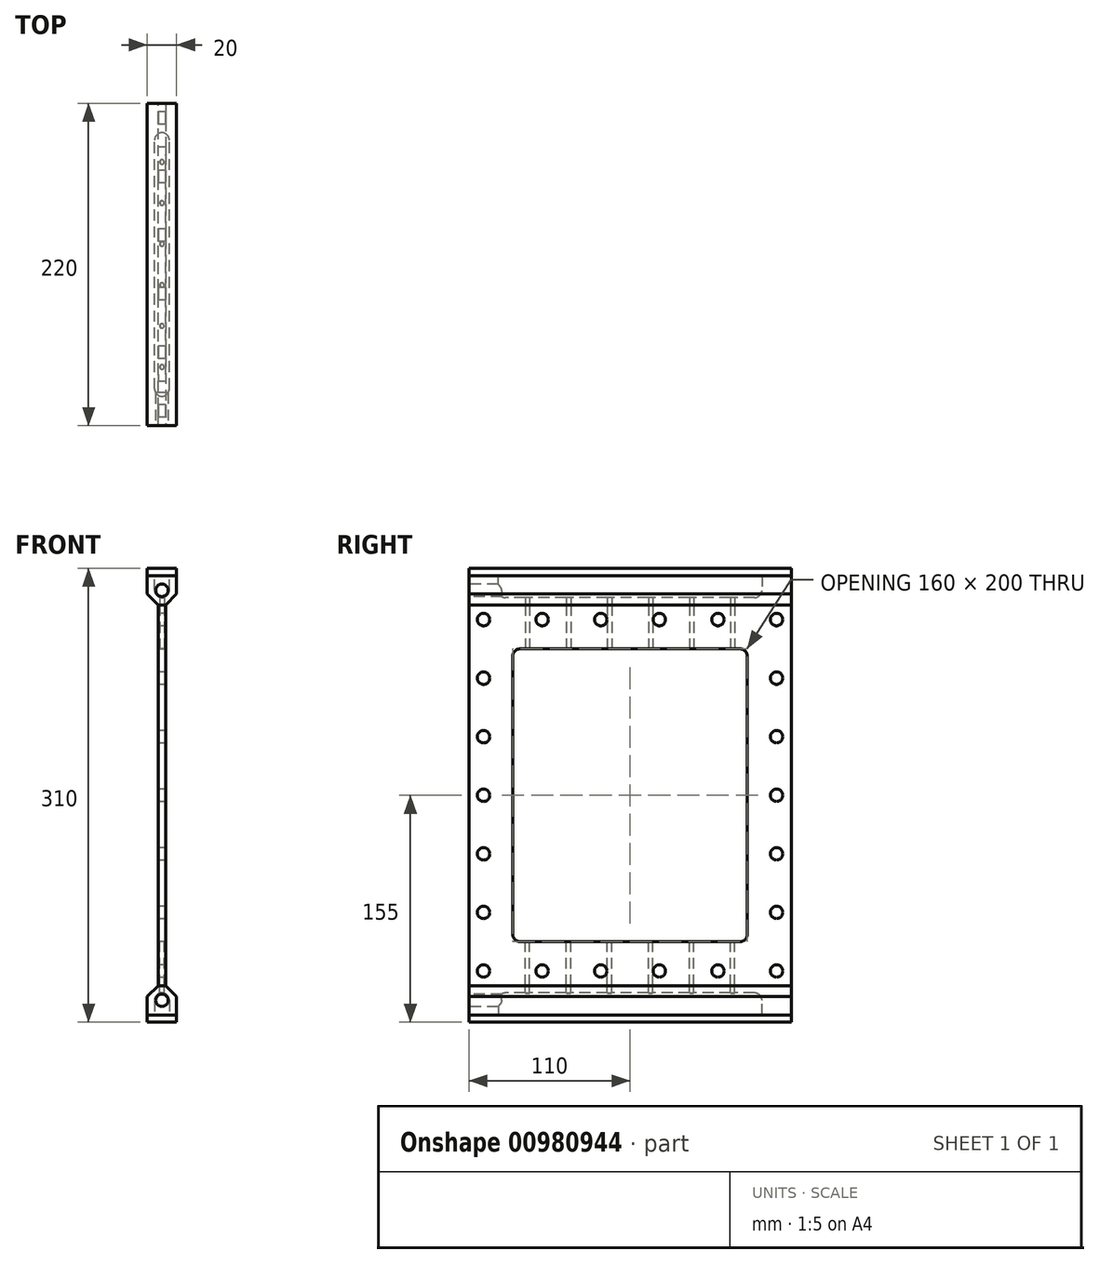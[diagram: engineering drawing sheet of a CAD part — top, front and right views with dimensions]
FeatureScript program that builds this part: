
annotation { "Feature Type Name" : "Feature", "Feature Type Description" : "" }
export const myFeature = defineFeature(function(context is Context, id is Id, definition is map)
    precondition{}
    {
        {
            var Q0;
            Q0=qCreatedBy(makeId("Right.planeOp"),FACE);
            var sketch = newSketch(context, id + "F0", { "sketchPlane" : qUnion([Q0])});
            skLineSegment(sketch, "E0.bottom", {"start": v(-80, 100) * mm, "end": v(80, 100) * mm});
            skLineSegment(sketch, "E0.top", {"start": v(-80, -100) * mm, "end": v(80, -100) * mm});
            skLineSegment(sketch, "E0.left", {"start": v(-80, 100) * mm, "end": v(-80, -100) * mm});
            skLineSegment(sketch, "E0.right", {"start": v(80, 100) * mm, "end": v(80, -100) * mm});
            skPoint(sketch, "E0.middle", {"position": v(0, 0) * mm});
            skLineSegment(sketch, "E1.0", {"start": v(-110, 130) * mm, "end": v(110, 130) * mm});
            skLineSegment(sketch, "E1.1", {"start": v(-110, 130) * mm, "end": v(-110, -130) * mm});
            skLineSegment(sketch, "E1.2", {"start": v(-110, -130) * mm, "end": v(110, -130) * mm});
            skLineSegment(sketch, "E1.3", {"start": v(110, 130) * mm, "end": v(110, -130) * mm});
            skLineSegment(sketch, "E2.0", {"start": v(-100, 120) * mm, "end": v(100, 120) * mm, "construction": true});
            skLineSegment(sketch, "E2.1", {"start": v(-100, 120) * mm, "end": v(-100, -120) * mm, "construction": true});
            skLineSegment(sketch, "E2.2", {"start": v(-100, -120) * mm, "end": v(100, -120) * mm, "construction": true});
            skLineSegment(sketch, "E2.3", {"start": v(100, 120) * mm, "end": v(100, -120) * mm, "construction": true});
            skCircle(sketch, "E3", {"center": v(-100, -120) * mm, "radius": 4.25 * mm});
            skCircle(sketch, "E4.0.1.0", {"center": v(-100, -80) * mm, "radius": 4.25 * mm});
            skCircle(sketch, "E4.0.2.0", {"center": v(-100, -40) * mm, "radius": 4.25 * mm});
            skCircle(sketch, "E4.0.3.0", {"center": v(-100, 0) * mm, "radius": 4.25 * mm});
            skCircle(sketch, "E4.0.4.0", {"center": v(-100, 40) * mm, "radius": 4.25 * mm});
            skCircle(sketch, "E4.0.5.0", {"center": v(-100, 80) * mm, "radius": 4.25 * mm});
            skCircle(sketch, "E4.0.6.0", {"center": v(-100, 120) * mm, "radius": 4.25 * mm});
            skLineSegment(sketch, "E4.direction1", {"start": v(-100, -120) * mm, "end": v(-60, -120) * mm, "construction": true});
            skLineSegment(sketch, "E4.direction2", {"start": v(-100, -120) * mm, "end": v(-100, -80) * mm, "construction": true});
            skCircle(sketch, "E5.1.0.0", {"center": v(-60, 120) * mm, "radius": 4.25 * mm});
            skCircle(sketch, "E5.2.0.0", {"center": v(-20, 120) * mm, "radius": 4.25 * mm});
            skCircle(sketch, "E5.3.0.0", {"center": v(20, 120) * mm, "radius": 4.25 * mm});
            skCircle(sketch, "E5.4.0.0", {"center": v(60, 120) * mm, "radius": 4.25 * mm});
            skCircle(sketch, "E5.5.0.0", {"center": v(100, 120) * mm, "radius": 4.25 * mm});
            skLineSegment(sketch, "E5.direction1", {"start": v(-100, 120) * mm, "end": v(-60, 120) * mm, "construction": true});
            skCircle(sketch, "E6.1.0.0", {"center": v(-60, -120) * mm, "radius": 4.25 * mm});
            skCircle(sketch, "E6.2.0.0", {"center": v(-20, -120) * mm, "radius": 4.25 * mm});
            skCircle(sketch, "E6.3.0.0", {"center": v(20, -120) * mm, "radius": 4.25 * mm});
            skCircle(sketch, "E6.4.0.0", {"center": v(60, -120) * mm, "radius": 4.25 * mm});
            skCircle(sketch, "E6.5.0.0", {"center": v(100, -120) * mm, "radius": 4.25 * mm});
            skCircle(sketch, "E7.1.0.0", {"center": v(100, 80) * mm, "radius": 4.25 * mm});
            skCircle(sketch, "E7.1.0.1", {"center": v(100, 40) * mm, "radius": 4.25 * mm});
            skCircle(sketch, "E7.1.0.2", {"center": v(100, 0) * mm, "radius": 4.25 * mm});
            skCircle(sketch, "E7.1.0.3", {"center": v(100, -40) * mm, "radius": 4.25 * mm});
            skCircle(sketch, "E7.1.0.4", {"center": v(100, -80) * mm, "radius": 4.25 * mm});
            skLineSegment(sketch, "E7.direction1", {"start": v(-100, 80) * mm, "end": v(100, 80) * mm, "construction": true});
            skSolve(sketch);
        }
        {
            var Q0;
            Q0 = qSketchRegion(id + "F0", true);
            extrude(context, id + "F1", {"entities" : qUnion([Q0]), "endBound" : BoundingType.SYMMETRIC, "depth" : 5 * mm, "offsetDistance" : 25 * mm});
        }
        {
            var Q0;
            Q0=makeQuery(id+"F1.opExtrude","SWEPT_FACE",FACE,{"disambiguationData":[OSD([sQuery(id+"F0.wireOp",EDGE,"E1.1")])]});
            var sketch = newSketch(context, id + "F2", { "sketchPlane" : qUnion([Q0])});
            skLineSegment(sketch, "E8", {"start": v(-10, 130) * mm, "end": v(10, 130) * mm});
            skLineSegment(sketch, "E9", {"start": v(10, 130) * mm, "end": v(10, 150) * mm});
            skLineSegment(sketch, "E10", {"start": v(10, 150) * mm, "end": v(-10, 150) * mm});
            skLineSegment(sketch, "E11", {"start": v(-10, 150) * mm, "end": v(-10, 130) * mm});
            skLineSegment(sketch, "E12", {"start": v(0, 150) * mm, "end": v(0, 130) * mm, "construction": true});
            skSolve(sketch);
        }
        {
            var Q0;
            Q0 = qSketchRegion(id + "F2", true);
            extrude(context, id + "F3", {"entities" : qUnion([Q0]), "oppositeDirection" : true, "depth" : 220 * mm, "offsetDistance" : 25 * mm});
        }
        {
            var Q0;
            Q0=makeQuery(id+"F3.opExtrude","SWEPT_FACE",FACE,{"disambiguationData":[OSD([sQuery(id+"F2.wireOp",EDGE,"E10")])]});
            var sketch = newSketch(context, id + "F4", { "sketchPlane" : qUnion([Q0])});
            skLineSegment(sketch, "E13.bottom", {"start": v(-5, -90) * mm, "end": v(5, -90) * mm});
            skLineSegment(sketch, "E13.top", {"start": v(-5, 90) * mm, "end": v(5, 90) * mm});
            skLineSegment(sketch, "E13.left", {"start": v(-5, -90) * mm, "end": v(-5, 90) * mm});
            skLineSegment(sketch, "E13.right", {"start": v(5, -90) * mm, "end": v(5, 90) * mm});
            skPoint(sketch, "E13.middle", {"position": v(0, 0) * mm});
            skSolve(sketch);
        }
        {
            var Q0;
            Q0=makeQuery(id+"F4.imprint","IMPRINT",FACE,{"disambiguationData":[TD([[makeQuery(id+"F4.imprint","IMPRINT",EDGE,{"derivedFrom":sQuery(id+"F4.wireOp",EDGE,"E13.bottom")}),1.0]])]});
            extrude(context, id + "F5", {"entities" : qUnion([Q0]), "operationType" : NewBodyOperationType.REMOVE, "oppositeDirection" : true, "depth" : 15 * mm, "offsetDistance" : 25 * mm});
        }
        {
            var Q0;
            Q0=makeQuery(id+"F5.boolean.opBoolean","COPY",FACE,{"derivedFrom":makeQuery(id+"F5.opExtrude","CAP_FACE",FACE,{"disambiguationData":[OSD([sQuery(id+"F4.wireOp",EDGE,"E13.bottom"),sQuery(id+"F4.wireOp",EDGE,"E13.top"),sQuery(id+"F4.wireOp",EDGE,"E13.left"),sQuery(id+"F4.wireOp",EDGE,"E13.right")])],"isStart":false})});
            var Q1;
            Q1=makeQuery(id+"F5.boolean.opBoolean","COPY",EDGE,{"derivedFrom":makeQuery(id+"F5.opExtrude","SWEPT_EDGE",EDGE,{"disambiguationData":[OSD([sQuery(id+"F4.wireOp",EDGE,"E13.top"),sQuery(id+"F4.wireOp",EDGE,"E13.left")])]})});
            var Q2;
            Q2=makeQuery(id+"F5.boolean.opBoolean","COPY",EDGE,{"derivedFrom":makeQuery(id+"F5.opExtrude","SWEPT_EDGE",EDGE,{"disambiguationData":[OSD([sQuery(id+"F4.wireOp",EDGE,"E13.top"),sQuery(id+"F4.wireOp",EDGE,"E13.right")])]})});
            var Q3;
            Q3=makeQuery(id+"F5.boolean.opBoolean","COPY",EDGE,{"derivedFrom":makeQuery(id+"F5.opExtrude","SWEPT_EDGE",EDGE,{"disambiguationData":[OSD([sQuery(id+"F4.wireOp",EDGE,"E13.bottom"),sQuery(id+"F4.wireOp",EDGE,"E13.left")])]})});
            var Q4;
            Q4=makeQuery(id+"F5.boolean.opBoolean","COPY",EDGE,{"derivedFrom":makeQuery(id+"F5.opExtrude","SWEPT_EDGE",EDGE,{"disambiguationData":[OSD([sQuery(id+"F4.wireOp",EDGE,"E13.bottom"),sQuery(id+"F4.wireOp",EDGE,"E13.right")])]})});
            fillet(context, id + "F6", {"entities" : qUnion([Q0, Q1, Q2, Q3, Q4]), "radius" : 5 * mm, "tangentPropagation" : true, "allowEdgeOverflow" : false});
        }
        {
            var Q0;
            Q0=makeQuery(id+"F3.opExtrude","SWEPT_EDGE",EDGE,{"disambiguationData":[OSD([sQuery(id+"F2.wireOp",EDGE,"E8"),sQuery(id+"F2.wireOp",EDGE,"E9")])]});
            var Q1;
            Q1=makeQuery(id+"F3.opExtrude","SWEPT_EDGE",EDGE,{"disambiguationData":[OSD([sQuery(id+"F2.wireOp",EDGE,"E8"),sQuery(id+"F2.wireOp",EDGE,"E11")])]});
            chamfer(context, id + "F7", {"entities" : qUnion([Q0, Q1]), "width" : 7.5 * mm, "tangentPropagation" : true});
        }
        {
            var Q0;
            Q0=makeQuery(id+"F3.opExtrude","CAP_FACE",FACE,{"disambiguationData":[OSD([sQuery(id+"F2.wireOp",EDGE,"E8"),sQuery(id+"F2.wireOp",EDGE,"E9"),sQuery(id+"F2.wireOp",EDGE,"E10"),sQuery(id+"F2.wireOp",EDGE,"E11")])],"isStart":true});
            var sketch = newSketch(context, id + "F8", { "sketchPlane" : qUnion([Q0])});
            skPoint(sketch, "E14", {"position": v(0, 140) * mm});
            skSolve(sketch);
        }
        {
            var Q0;
            Q0=sQuery(id+"F8.wireOp",VERTEX,"E14");
            var Q1;
            Q1=makeQuery(id+"F3.opExtrude","SWEPT_BODY",BODY,{"disambiguationData":[OSD([sQuery(id+"F2.wireOp",EDGE,"E8"),sQuery(id+"F2.wireOp",EDGE,"E9"),sQuery(id+"F2.wireOp",EDGE,"E10"),sQuery(id+"F2.wireOp",EDGE,"E11")])]});
            hole(context, id + "F9", {"style" : HoleStyle.SIMPLE, "endStyle" : HoleEndStyle.BLIND, "standardTappedOrClearance" : lookupTablePath({ "standard" : "ISO", "engagement" : "75%", "pitch" : "1.5 mm", "size" : "M10", "type" : "Tapped" }), "standardBlindInLast" : lookupTablePath({ "standard" : "ISO", "fit" : "Normal", "engagement" : "75%", "pitch" : "1.5 mm", "size" : "M10", "type" : "Clearance & tapped" }), "holeDiameter" : 8.5 * mm, "majorDiameter" : 10 * mm, "showTappedDepth" : true, "holeDepth" : 29.5 * mm, "tappedDepth" : 25 * mm, "tapClearance" : 3, "startFromSketch" : true, "locations" : qUnion([Q0]), "scope" : qUnion([Q1])});
        }
        {
            var Q0;
            Q0=makeQuery(id+"F3.opExtrude","SWEPT_BODY",BODY,{"disambiguationData":[OSD([sQuery(id+"F2.wireOp",EDGE,"E8"),sQuery(id+"F2.wireOp",EDGE,"E9"),sQuery(id+"F2.wireOp",EDGE,"E10"),sQuery(id+"F2.wireOp",EDGE,"E11")])]});
            var Q1;
            Q1=qCreatedBy(makeId("Top.planeOp"),FACE);
            mirror(context, id + "F10", {"entities" : qUnion([Q0]), "mirrorPlane" : qUnion([Q1])});
        }
        {
            var Q0;
            Q0=makeQuery(id+"F4.imprint","IMPRINT",FACE,{"disambiguationData":[TD([[makeQuery(id+"F4.imprint","IMPRINT",EDGE,{"derivedFrom":sQuery(id+"F4.wireOp",EDGE,"E13.bottom")}),-1.0]])]});
            var Q1;
            Q1=makeQuery(id+"F4.imprint","IMPRINT",FACE,{"disambiguationData":[TD([[makeQuery(id+"F4.imprint","IMPRINT",EDGE,{"derivedFrom":sQuery(id+"F4.wireOp",EDGE,"E13.bottom")}),1.0]])]});
            extrude(context, id + "F11", {"entities" : qUnion([Q0, Q1]), "depth" : 5 * mm, "offsetDistance" : 25 * mm});
        }
        {
            var Q0;
            Q0=makeQuery(id+"F1.opExtrude","SWEPT_FACE",FACE,{"disambiguationData":[OSD([sQuery(id+"F0.wireOp",EDGE,"E0.bottom")])]});
            var sketch = newSketch(context, id + "F12", { "sketchPlane" : qUnion([Q0])});
            skPoint(sketch, "E15", {"position": v(0, -70) * mm});
            skPoint(sketch, "E16.0.1.0", {"position": v(0, -42) * mm});
            skPoint(sketch, "E16.0.2.0", {"position": v(0, -14) * mm});
            skPoint(sketch, "E16.0.3.0", {"position": v(0, 14) * mm});
            skPoint(sketch, "E16.0.4.0", {"position": v(0, 42) * mm});
            skPoint(sketch, "E16.0.5.0", {"position": v(0, 70) * mm});
            skLineSegment(sketch, "E16.direction1", {"start": v(0, -70) * mm, "end": v(25, -70) * mm, "construction": true});
            skLineSegment(sketch, "E16.direction2", {"start": v(0, -70) * mm, "end": v(0, -42) * mm, "construction": true});
            skSolve(sketch);
        }
        {
            var Q0;
            Q0=sQuery(id+"F12.wireOp",VERTEX,"E15");
            var Q1;
            Q1=sQuery(id+"F12.wireOp",VERTEX,"E16.0.1.0");
            var Q2;
            Q2=sQuery(id+"F12.wireOp",VERTEX,"E16.0.2.0");
            var Q3;
            Q3=sQuery(id+"F12.wireOp",VERTEX,"E16.0.3.0");
            var Q4;
            Q4=sQuery(id+"F12.wireOp",VERTEX,"E16.0.4.0");
            var Q5;
            Q5=sQuery(id+"F12.wireOp",VERTEX,"E16.0.5.0");
            var Q6;
            Q6=makeQuery(id+"F3.opExtrude","SWEPT_BODY",BODY,{"disambiguationData":[OSD([sQuery(id+"F2.wireOp",EDGE,"E8"),sQuery(id+"F2.wireOp",EDGE,"E9"),sQuery(id+"F2.wireOp",EDGE,"E10"),sQuery(id+"F2.wireOp",EDGE,"E11")])]});
            var Q7;
            Q7=makeQuery(id+"F1.opExtrude","SWEPT_BODY",BODY,{"disambiguationData":[OSD([sQuery(id+"F0.wireOp",EDGE,"E0.bottom"),sQuery(id+"F0.wireOp",EDGE,"E0.top"),sQuery(id+"F0.wireOp",EDGE,"E0.left"),sQuery(id+"F0.wireOp",EDGE,"E0.right"),sQuery(id+"F0.wireOp",EDGE,"E1.0"),sQuery(id+"F0.wireOp",EDGE,"E1.1"),sQuery(id+"F0.wireOp",EDGE,"E1.2"),sQuery(id+"F0.wireOp",EDGE,"E1.3"),sQuery(id+"F0.wireOp",EDGE,"E3"),sQuery(id+"F0.wireOp",EDGE,"E4.0.1.0"),sQuery(id+"F0.wireOp",EDGE,"E4.0.2.0"),sQuery(id+"F0.wireOp",EDGE,"E4.0.3.0"),sQuery(id+"F0.wireOp",EDGE,"E4.0.4.0"),sQuery(id+"F0.wireOp",EDGE,"E4.0.5.0"),sQuery(id+"F0.wireOp",EDGE,"E4.0.6.0"),sQuery(id+"F0.wireOp",EDGE,"E5.1.0.0"),sQuery(id+"F0.wireOp",EDGE,"E5.2.0.0"),sQuery(id+"F0.wireOp",EDGE,"E5.3.0.0"),sQuery(id+"F0.wireOp",EDGE,"E5.4.0.0"),sQuery(id+"F0.wireOp",EDGE,"E5.5.0.0"),sQuery(id+"F0.wireOp",EDGE,"E6.1.0.0"),sQuery(id+"F0.wireOp",EDGE,"E6.2.0.0"),sQuery(id+"F0.wireOp",EDGE,"E6.3.0.0"),sQuery(id+"F0.wireOp",EDGE,"E6.4.0.0"),sQuery(id+"F0.wireOp",EDGE,"E6.5.0.0"),sQuery(id+"F0.wireOp",EDGE,"E7.1.0.0"),sQuery(id+"F0.wireOp",EDGE,"E7.1.0.1"),sQuery(id+"F0.wireOp",EDGE,"E7.1.0.2"),sQuery(id+"F0.wireOp",EDGE,"E7.1.0.3"),sQuery(id+"F0.wireOp",EDGE,"E7.1.0.4")])]});
            hole(context, id + "F13", {"style" : HoleStyle.SIMPLE, "endStyle" : HoleEndStyle.BLIND, "standardTappedOrClearance" : lookupTablePath({ "standard" : "ISO", "size" : "3", "type" : "Drilled" }), "standardBlindInLast" : lookupTablePath({ "standard" : "ISO", "size" : "3", "type" : "Drilled" }), "holeDiameter" : 3 * mm, "majorDiameter" : 5 * mm, "holeDepth" : 35 * mm, "tappedDepth" : 25 * mm, "tapClearance" : 3, "startFromSketch" : true, "locations" : qUnion([Q0, Q1, Q2, Q3, Q4, Q5]), "scope" : qUnion([Q6, Q7])});
        }
        {
            var Q0;
            Q0=makeQuery(id+"F1.opExtrude","SWEPT_FACE",FACE,{"disambiguationData":[OSD([sQuery(id+"F0.wireOp",EDGE,"E0.top")])]});
            var sketch = newSketch(context, id + "F14", { "sketchPlane" : qUnion([Q0])});
            skPoint(sketch, "E17", {"position": v(0, 70) * mm});
            skPoint(sketch, "E18.0.1.0", {"position": v(0, 42) * mm});
            skPoint(sketch, "E18.0.2.0", {"position": v(0, 14) * mm});
            skPoint(sketch, "E18.0.3.0", {"position": v(0, -14) * mm});
            skPoint(sketch, "E18.0.4.0", {"position": v(0, -42) * mm});
            skPoint(sketch, "E18.0.5.0", {"position": v(0, -70) * mm});
            skLineSegment(sketch, "E18.direction1", {"start": v(0, 70) * mm, "end": v(25, 70) * mm, "construction": true});
            skLineSegment(sketch, "E18.direction2", {"start": v(0, 70) * mm, "end": v(0, 42) * mm, "construction": true});
            skSolve(sketch);
        }
        {
            var Q0;
            Q0=sQuery(id+"F14.wireOp",VERTEX,"E17");
            var Q1;
            Q1=sQuery(id+"F14.wireOp",VERTEX,"E18.0.1.0");
            var Q2;
            Q2=sQuery(id+"F14.wireOp",VERTEX,"E18.0.2.0");
            var Q3;
            Q3=sQuery(id+"F14.wireOp",VERTEX,"E18.0.3.0");
            var Q4;
            Q4=sQuery(id+"F14.wireOp",VERTEX,"E18.0.4.0");
            var Q5;
            Q5=sQuery(id+"F14.wireOp",VERTEX,"E18.0.5.0");
            var Q6;
            Q6=makeQuery(id+"F1.opExtrude","SWEPT_BODY",BODY,{"disambiguationData":[OSD([sQuery(id+"F0.wireOp",EDGE,"E0.bottom"),sQuery(id+"F0.wireOp",EDGE,"E0.top"),sQuery(id+"F0.wireOp",EDGE,"E0.left"),sQuery(id+"F0.wireOp",EDGE,"E0.right"),sQuery(id+"F0.wireOp",EDGE,"E1.0"),sQuery(id+"F0.wireOp",EDGE,"E1.1"),sQuery(id+"F0.wireOp",EDGE,"E1.2"),sQuery(id+"F0.wireOp",EDGE,"E1.3"),sQuery(id+"F0.wireOp",EDGE,"E3"),sQuery(id+"F0.wireOp",EDGE,"E4.0.1.0"),sQuery(id+"F0.wireOp",EDGE,"E4.0.2.0"),sQuery(id+"F0.wireOp",EDGE,"E4.0.3.0"),sQuery(id+"F0.wireOp",EDGE,"E4.0.4.0"),sQuery(id+"F0.wireOp",EDGE,"E4.0.5.0"),sQuery(id+"F0.wireOp",EDGE,"E4.0.6.0"),sQuery(id+"F0.wireOp",EDGE,"E5.1.0.0"),sQuery(id+"F0.wireOp",EDGE,"E5.2.0.0"),sQuery(id+"F0.wireOp",EDGE,"E5.3.0.0"),sQuery(id+"F0.wireOp",EDGE,"E5.4.0.0"),sQuery(id+"F0.wireOp",EDGE,"E5.5.0.0"),sQuery(id+"F0.wireOp",EDGE,"E6.1.0.0"),sQuery(id+"F0.wireOp",EDGE,"E6.2.0.0"),sQuery(id+"F0.wireOp",EDGE,"E6.3.0.0"),sQuery(id+"F0.wireOp",EDGE,"E6.4.0.0"),sQuery(id+"F0.wireOp",EDGE,"E6.5.0.0"),sQuery(id+"F0.wireOp",EDGE,"E7.1.0.0"),sQuery(id+"F0.wireOp",EDGE,"E7.1.0.1"),sQuery(id+"F0.wireOp",EDGE,"E7.1.0.2"),sQuery(id+"F0.wireOp",EDGE,"E7.1.0.3"),sQuery(id+"F0.wireOp",EDGE,"E7.1.0.4")])]});
            var Q7;
            Q7=makeQuery(id+"F10.opPattern","COPY",BODY,{"derivedFrom":makeQuery(id+"F3.opExtrude","SWEPT_BODY",BODY,{"disambiguationData":[OSD([sQuery(id+"F2.wireOp",EDGE,"E8"),sQuery(id+"F2.wireOp",EDGE,"E9"),sQuery(id+"F2.wireOp",EDGE,"E10"),sQuery(id+"F2.wireOp",EDGE,"E11")])]}),"instanceName":"1"});
            hole(context, id + "F15", {"style" : HoleStyle.SIMPLE, "endStyle" : HoleEndStyle.BLIND, "standardTappedOrClearance" : lookupTablePath({ "standard" : "ISO", "size" : "3", "type" : "Drilled" }), "standardBlindInLast" : lookupTablePath({ "standard" : "ISO", "size" : "3", "type" : "Drilled" }), "holeDiameter" : 3 * mm, "majorDiameter" : 5 * mm, "holeDepth" : 35 * mm, "tappedDepth" : 25 * mm, "tapClearance" : 3, "startFromSketch" : true, "locations" : qUnion([Q0, Q1, Q2, Q3, Q4, Q5]), "scope" : qUnion([Q6, Q7])});
        }
        {
            var Q0;
            Q0=makeQuery(id+"F11.opExtrude","SWEPT_BODY",BODY,{"disambiguationData":[OSD([sQuery(id+"F2.wireOp",EDGE,"E9"),sQuery(id+"F2.wireOp",EDGE,"E10"),sQuery(id+"F2.wireOp",EDGE,"E11")])]});
            var Q1;
            Q1=qCreatedBy(makeId("Top.planeOp"),FACE);
            mirror(context, id + "F16", {"entities" : qUnion([Q0]), "mirrorPlane" : qUnion([Q1])});
        }
        {
            var Q0;
            Q0=makeQuery(id+"F1.opExtrude","SWEPT_EDGE",EDGE,{"disambiguationData":[OSD([sQuery(id+"F0.wireOp",EDGE,"E0.bottom"),sQuery(id+"F0.wireOp",EDGE,"E0.right")])]});
            var Q1;
            Q1=makeQuery(id+"F1.opExtrude","SWEPT_EDGE",EDGE,{"disambiguationData":[OSD([sQuery(id+"F0.wireOp",EDGE,"E0.bottom"),sQuery(id+"F0.wireOp",EDGE,"E0.left")])]});
            var Q2;
            Q2=makeQuery(id+"F1.opExtrude","SWEPT_EDGE",EDGE,{"disambiguationData":[OSD([sQuery(id+"F0.wireOp",EDGE,"E0.top"),sQuery(id+"F0.wireOp",EDGE,"E0.right")])]});
            var Q3;
            Q3=makeQuery(id+"F1.opExtrude","SWEPT_EDGE",EDGE,{"disambiguationData":[OSD([sQuery(id+"F0.wireOp",EDGE,"E0.top"),sQuery(id+"F0.wireOp",EDGE,"E0.left")])]});
            fillet(context, id + "F17", {"entities" : qUnion([Q0, Q1, Q2, Q3]), "radius" : 5 * mm, "tangentPropagation" : true, "allowEdgeOverflow" : false});
        }
    });
